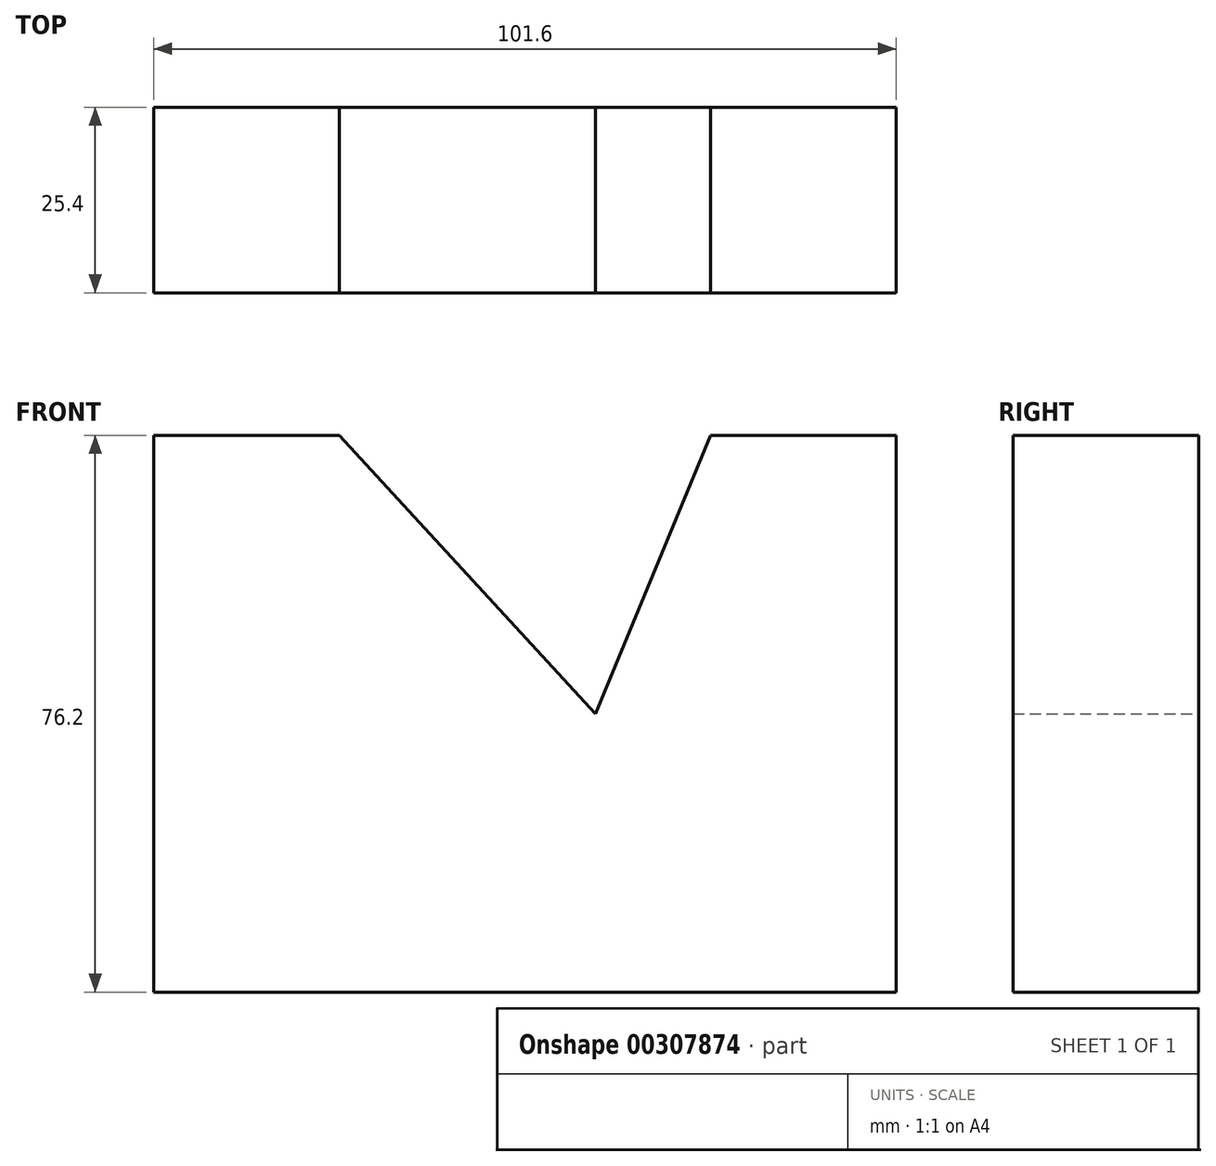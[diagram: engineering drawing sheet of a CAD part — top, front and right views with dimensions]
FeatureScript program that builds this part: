
annotation { "Feature Type Name" : "Feature", "Feature Type Description" : "" }
export const myFeature = defineFeature(function(context is Context, id is Id, definition is map)
    precondition{}
    {
        {
            var Q0;
            Q0=qCreatedBy(makeId("Front.planeOp"),FACE);
            var sketch = newSketch(context, id + "F0", { "sketchPlane" : qUnion([Q0])});
            skLineSegment(sketch, "E0", {"start": v(-31.5, 20.57) * mm, "end": v(-56.9, 20.57) * mm});
            skLineSegment(sketch, "E1", {"start": v(-56.9, 20.57) * mm, "end": v(-56.9, -55.63) * mm});
            skLineSegment(sketch, "E2", {"start": v(-56.9, -55.63) * mm, "end": v(44.7, -55.63) * mm});
            skLineSegment(sketch, "E3", {"start": v(44.7, -55.63) * mm, "end": v(44.7, 20.57) * mm});
            skLineSegment(sketch, "E4", {"start": v(44.7, 20.57) * mm, "end": v(19.3, 20.57) * mm});
            skLineSegment(sketch, "E5", {"start": v(3.57, -17.53) * mm, "end": v(-31.5, 20.57) * mm});
            skLineSegment(sketch, "E6", {"start": v(3.57, -17.53) * mm, "end": v(19.3, 20.57) * mm});
            skSolve(sketch);
        }
        {
            var Q0;
            Q0=makeQuery(id+"F0.imprint","IMPRINT",FACE,{"disambiguationData":[TD([[makeQuery(id+"F0.imprint","IMPRINT",EDGE,{"derivedFrom":sQuery(id+"F0.wireOp",EDGE,"E0")}),1.0]])]});
            extrude(context, id + "F1", {"entities" : qUnion([Q0]), "depth" : 25.4 * mm});
        }
    });
